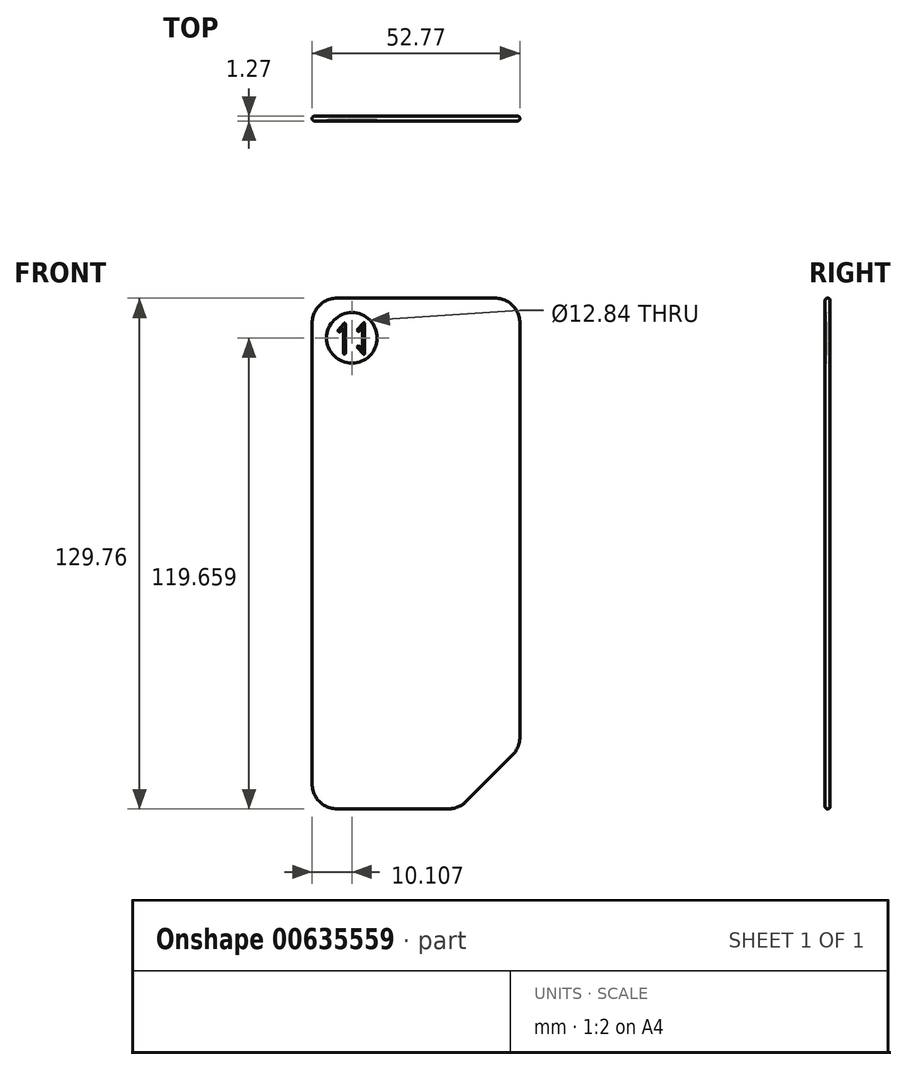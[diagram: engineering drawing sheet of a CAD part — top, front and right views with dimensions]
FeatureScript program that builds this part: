
annotation { "Feature Type Name" : "Feature", "Feature Type Description" : "" }
export const myFeature = defineFeature(function(context is Context, id is Id, definition is map)
    precondition{}
    {
        {
            var Q0;
            Q0=qCreatedBy(makeId("Front.planeOp"),FACE);
            var sketch = newSketch(context, id + "F0", { "sketchPlane" : qUnion([Q0])});
            skLineSegment(sketch, "E0.bottom", {"start": v(-53.55, 59.75) * mm, "end": v(-13.48, 59.75) * mm});
            skLineSegment(sketch, "E0.top", {"start": v(-53.55, -70) * mm, "end": v(-25.3, -70) * mm});
            skLineSegment(sketch, "E0.left", {"start": v(-59.9, 53.4) * mm, "end": v(-59.9, -63.66) * mm});
            skLineSegment(sketch, "E0.right", {"start": v(-7.13, 53.4) * mm, "end": v(-7.13, -51.85) * mm});
            skPoint(sketch, "E1.visualSharp", {"position": v(-7.13, 59.75) * mm});
            skArc(sketch, "E1.filletArc", {"start": v(-7.13, 53.4) * mm, "mid": v(-8.99, 57.9) * mm, "end": v(-13.48, 59.75) * mm});
            skPoint(sketch, "E2.visualSharp", {"position": v(-59.9, 59.75) * mm});
            skArc(sketch, "E2.filletArc", {"start": v(-53.55, 59.75) * mm, "mid": v(-58.04, 57.9) * mm, "end": v(-59.9, 53.4) * mm});
            skPoint(sketch, "E3.visualSharp", {"position": v(-59.9, -70) * mm});
            skArc(sketch, "E3.filletArc", {"start": v(-59.9, -63.66) * mm, "mid": v(-58.04, -68.15) * mm, "end": v(-53.55, -70) * mm});
            skPoint(sketch, "E4.visualSharp", {"position": v(-7.13, -70) * mm});
            skLineSegment(sketch, "E5", {"start": v(-20.8, -68.15) * mm, "end": v(-8.99, -56.34) * mm});
            skPoint(sketch, "E6.visualSharp", {"position": v(-7.13, -54.48) * mm});
            skArc(sketch, "E6.filletArc", {"start": v(-8.99, -56.34) * mm, "mid": v(-7.61, -54.28) * mm, "end": v(-7.13, -51.85) * mm});
            skPoint(sketch, "E7.visualSharp", {"position": v(-22.66, -70) * mm});
            skArc(sketch, "E7.filletArc", {"start": v(-25.3, -70) * mm, "mid": v(-22.86, -69.53) * mm, "end": v(-20.8, -68.15) * mm});
            skSolve(sketch);
        }
        {
            var Q0;
            Q0 = qSketchRegion(id + "F0", true);
            extrude(context, id + "F1", {"entities" : qUnion([Q0]), "depth" : 1.27 * mm, "offsetDistance" : 25.4 * mm});
        }
        {
            var Q0;
            Q0=qCreatedBy(makeId("Front.planeOp"),FACE);
            var sketch = newSketch(context, id + "F2", { "sketchPlane" : qUnion([Q0])});
            skLineSegment(sketch, "E8", {"start": v(0, -48.41) * mm, "end": v(-28.1, -76.5) * mm});
            skLineSegment(sketch, "E9", {"start": v(-28.1, -76.5) * mm, "end": v(0, -76.5) * mm});
            skLineSegment(sketch, "E10", {"start": v(0, -76.5) * mm, "end": v(0, -48.41) * mm});
            skSolve(sketch);
        }
        {
            var Q0;
            Q0 = qSketchRegion(id + "F2", true);
            extrude(context, id + "F3", {"entities" : qUnion([Q0]), "operationType" : NewBodyOperationType.REMOVE, "depth" : 25.4 * mm, "offsetDistance" : 25.4 * mm});
        }
        {
            var Q0;
            Q0=makeQuery(id+"F1.opExtrude","CAP_FACE",FACE,{"disambiguationData":[OSD([sQuery(id+"F0.wireOp",EDGE,"E0.bottom"),sQuery(id+"F0.wireOp",EDGE,"E0.top"),sQuery(id+"F0.wireOp",EDGE,"E0.left"),sQuery(id+"F0.wireOp",EDGE,"E0.right"),sQuery(id+"F0.wireOp",EDGE,"E1.filletArc"),sQuery(id+"F0.wireOp",EDGE,"E2.filletArc"),sQuery(id+"F0.wireOp",EDGE,"E3.filletArc"),sQuery(id+"F0.wireOp",EDGE,"E4.filletArc")])],"isStart":false});
            var Q1;
            Q1=makeQuery(id+"F1.opExtrude","CAP_FACE",FACE,{"disambiguationData":[OSD([sQuery(id+"F0.wireOp",EDGE,"E0.bottom"),sQuery(id+"F0.wireOp",EDGE,"E0.top"),sQuery(id+"F0.wireOp",EDGE,"E0.left"),sQuery(id+"F0.wireOp",EDGE,"E0.right"),sQuery(id+"F0.wireOp",EDGE,"E1.filletArc"),sQuery(id+"F0.wireOp",EDGE,"E2.filletArc"),sQuery(id+"F0.wireOp",EDGE,"E3.filletArc"),sQuery(id+"F0.wireOp",EDGE,"E4.filletArc")])],"isStart":true});
            fillet(context, id + "F4", {"entities" : qUnion([Q0, Q1]), "radius" : 0.64 * mm, "tangentPropagation" : true, "allowEdgeOverflow" : false});
        }
        {
            var Q0;
            Q0=makeQuery(id+"F1.opExtrude","CAP_FACE",FACE,{"disambiguationData":[OSD([sQuery(id+"F0.wireOp",EDGE,"E0.bottom"),sQuery(id+"F0.wireOp",EDGE,"E0.top"),sQuery(id+"F0.wireOp",EDGE,"E0.left"),sQuery(id+"F0.wireOp",EDGE,"E0.right"),sQuery(id+"F0.wireOp",EDGE,"E1.filletArc"),sQuery(id+"F0.wireOp",EDGE,"E2.filletArc"),sQuery(id+"F0.wireOp",EDGE,"E3.filletArc"),sQuery(id+"F0.wireOp",EDGE,"E5"),sQuery(id+"F0.wireOp",EDGE,"E6.filletArc"),sQuery(id+"F0.wireOp",EDGE,"E7.filletArc")])],"isStart":false});
            var sketch = newSketch(context, id + "F5", { "sketchPlane" : qUnion([Q0])});
            skCircle(sketch, "E11", {"center": v(-49.8, 49.65) * mm, "radius": 6.42 * mm});
            skLineSegment(sketch, "E12", {"start": v(-48.47, 47.32) * mm, "end": v(-46.9, 45.52) * mm});
            skLineSegment(sketch, "E13", {"start": v(-46.58, 45.64) * mm, "end": v(-46.58, 49.5) * mm});
            skLineSegment(sketch, "E14", {"start": v(-47.06, 49.5) * mm, "end": v(-47.06, 47.02) * mm});
            skLineSegment(sketch, "E15", {"start": v(-47.39, 46.9) * mm, "end": v(-48.1, 47.7) * mm});
            skLineSegment(sketch, "E16", {"start": v(-48.1, 47.7) * mm, "end": v(-48.47, 47.32) * mm});
            skPoint(sketch, "E17.visualSharp", {"position": v(-47.06, 46.53) * mm});
            skArc(sketch, "E17.filletArc", {"start": v(-47.39, 46.9) * mm, "mid": v(-47.18, 46.85) * mm, "end": v(-47.06, 47.02) * mm});
            skPoint(sketch, "E18.visualSharp", {"position": v(-46.58, 45.14) * mm});
            skArc(sketch, "E18.filletArc", {"start": v(-46.9, 45.52) * mm, "mid": v(-46.7, 45.47) * mm, "end": v(-46.58, 45.64) * mm});
            skLineSegment(sketch, "E19.MirrorCS", {"start": v(-46.58, 53.34) * mm, "end": v(-46.58, 49.5) * mm});
            skLineSegment(sketch, "E20.MirrorCS", {"start": v(-47.06, 49.5) * mm, "end": v(-47.06, 51.96) * mm});
            skLineSegment(sketch, "E21.MirrorCS", {"start": v(-48.1, 51.29) * mm, "end": v(-48.47, 51.66) * mm});
            skLineSegment(sketch, "E22.MirrorCS", {"start": v(-48.47, 51.66) * mm, "end": v(-46.9, 53.47) * mm});
            skArc(sketch, "E23.MirrorCS", {"start": v(-46.9, 53.47) * mm, "mid": v(-46.7, 53.52) * mm, "end": v(-46.58, 53.34) * mm});
            skArc(sketch, "E24.MirrorCS", {"start": v(-47.39, 52.09) * mm, "mid": v(-47.18, 52.14) * mm, "end": v(-47.06, 51.96) * mm});
            skLineSegment(sketch, "E25.MirrorCS", {"start": v(-47.39, 52.09) * mm, "end": v(-48.1, 51.29) * mm});
            skLineSegment(sketch, "E26", {"start": v(-51.47, 45.69) * mm, "end": v(-51.47, 51.3) * mm});
            skLineSegment(sketch, "E27", {"start": v(-51.95, 51.3) * mm, "end": v(-51.95, 46.88) * mm});
            skPoint(sketch, "E28.visualSharp", {"position": v(-51.95, 46.38) * mm});
            skPoint(sketch, "E29.visualSharp", {"position": v(-51.47, 45) * mm});
            skLineSegment(sketch, "E30.MirrorCS", {"start": v(-51.47, 53.2) * mm, "end": v(-51.47, 49.35) * mm});
            skLineSegment(sketch, "E31.MirrorCS", {"start": v(-51.95, 49.35) * mm, "end": v(-51.95, 51.82) * mm});
            skLineSegment(sketch, "E32.MirrorCS", {"start": v(-53, 51.15) * mm, "end": v(-53.37, 51.52) * mm});
            skLineSegment(sketch, "E33.MirrorCS", {"start": v(-53.37, 51.52) * mm, "end": v(-51.8, 53.32) * mm});
            skLineSegment(sketch, "E34.MirrorCS", {"start": v(-52.28, 51.95) * mm, "end": v(-53, 51.15) * mm});
            skArc(sketch, "E35", {"start": v(-51.47, 53.2) * mm, "mid": v(-51.6, 53.37) * mm, "end": v(-51.8, 53.32) * mm});
            skArc(sketch, "E36", {"start": v(-51.95, 51.82) * mm, "mid": v(-52.07, 52) * mm, "end": v(-52.28, 51.95) * mm});
            skLineSegment(sketch, "E37.bottom", {"start": v(-51.66, 45.5) * mm, "end": v(-51.76, 45.5) * mm});
            skLineSegment(sketch, "E37.left", {"start": v(-51.47, 45.5) * mm, "end": v(-51.47, 46.88) * mm});
            skLineSegment(sketch, "E37.right", {"start": v(-51.95, 45.69) * mm, "end": v(-51.95, 46.88) * mm});
            skPoint(sketch, "E38.visualSharp", {"position": v(-51.95, 45.5) * mm});
            skArc(sketch, "E38.filletArc", {"start": v(-51.95, 45.69) * mm, "mid": v(-51.9, 45.56) * mm, "end": v(-51.76, 45.5) * mm});
            skPoint(sketch, "E39.visualSharp", {"position": v(-51.47, 45.5) * mm});
            skArc(sketch, "E39.filletArc", {"start": v(-51.66, 45.5) * mm, "mid": v(-51.53, 45.56) * mm, "end": v(-51.47, 45.69) * mm});
            skSolve(sketch);
        }
        {
            var Q0;
            Q0=makeQuery(id+"F5.imprint","IMPRINT",FACE,{"disambiguationData":[TD([[makeQuery(id+"F5.imprint","IMPRINT",EDGE,{"derivedFrom":sQuery(id+"F5.wireOp",EDGE,"E11")}),1.0]])]});
            extrude(context, id + "F6", {"entities" : qUnion([Q0]), "operationType" : NewBodyOperationType.REMOVE, "oppositeDirection" : true, "depth" : 0.38 * mm, "offsetDistance" : 25.4 * mm});
        }
        {
            var Q0;
            Q0=makeQuery(id+"F6.boolean.opBoolean","COPY",EDGE,{"derivedFrom":makeQuery(id+"F6.opExtrude","CAP_EDGE",EDGE,{"disambiguationData":[OSD([sQuery(id+"F5.wireOp",EDGE,"E11")])],"isStart":false})});
            var Q1;
            Q1=makeQuery(id+"F6.boolean.opBoolean","COPY",EDGE,{"derivedFrom":makeQuery(id+"F6.opExtrude","CAP_EDGE",EDGE,{"disambiguationData":[OSD([sQuery(id+"F5.wireOp",EDGE,"E11")])],"isStart":true})});
            var Q2;
            Q2=makeQuery(id+"F6.boolean.opBoolean","SPLIT",FACE,{"disambiguationData":[TD([makeQuery(id+"F6.opExtrude","SWEPT_FACE",FACE,{"disambiguationData":[OSD([sQuery(id+"F5.wireOp",EDGE,"E32.MirrorCS")])]})])],"derivedFrom":makeQuery(id+"F1.opExtrude","CAP_FACE",FACE,{"disambiguationData":[OSD([sQuery(id+"F0.wireOp",EDGE,"E0.bottom"),sQuery(id+"F0.wireOp",EDGE,"E0.top"),sQuery(id+"F0.wireOp",EDGE,"E0.left"),sQuery(id+"F0.wireOp",EDGE,"E0.right"),sQuery(id+"F0.wireOp",EDGE,"E1.filletArc"),sQuery(id+"F0.wireOp",EDGE,"E2.filletArc"),sQuery(id+"F0.wireOp",EDGE,"E3.filletArc"),sQuery(id+"F0.wireOp",EDGE,"E5"),sQuery(id+"F0.wireOp",EDGE,"E6.filletArc"),sQuery(id+"F0.wireOp",EDGE,"E7.filletArc")])],"isStart":false})});
            var Q3;
            Q3=makeQuery(id+"F6.boolean.opBoolean","SPLIT",FACE,{"disambiguationData":[TD([makeQuery(id+"F6.opExtrude","SWEPT_FACE",FACE,{"disambiguationData":[OSD([sQuery(id+"F5.wireOp",EDGE,"E12")])]})])],"derivedFrom":makeQuery(id+"F1.opExtrude","CAP_FACE",FACE,{"disambiguationData":[OSD([sQuery(id+"F0.wireOp",EDGE,"E0.bottom"),sQuery(id+"F0.wireOp",EDGE,"E0.top"),sQuery(id+"F0.wireOp",EDGE,"E0.left"),sQuery(id+"F0.wireOp",EDGE,"E0.right"),sQuery(id+"F0.wireOp",EDGE,"E1.filletArc"),sQuery(id+"F0.wireOp",EDGE,"E2.filletArc"),sQuery(id+"F0.wireOp",EDGE,"E3.filletArc"),sQuery(id+"F0.wireOp",EDGE,"E5"),sQuery(id+"F0.wireOp",EDGE,"E6.filletArc"),sQuery(id+"F0.wireOp",EDGE,"E7.filletArc")])],"isStart":false})});
            var Q4;
            Q4=makeQuery(id+"F6.boolean.opBoolean","COPY",FACE,{"derivedFrom":makeQuery(id+"F6.opExtrude","CAP_FACE",FACE,{"disambiguationData":[OSD([sQuery(id+"F5.wireOp",EDGE,"E11"),sQuery(id+"F5.wireOp",EDGE,"E12"),sQuery(id+"F5.wireOp",EDGE,"E13"),sQuery(id+"F5.wireOp",EDGE,"E14"),sQuery(id+"F5.wireOp",EDGE,"E15"),sQuery(id+"F5.wireOp",EDGE,"E16"),sQuery(id+"F5.wireOp",EDGE,"E17.filletArc"),sQuery(id+"F5.wireOp",EDGE,"E18.filletArc"),sQuery(id+"F5.wireOp",EDGE,"E19.MirrorCS"),sQuery(id+"F5.wireOp",EDGE,"E20.MirrorCS"),sQuery(id+"F5.wireOp",EDGE,"E21.MirrorCS"),sQuery(id+"F5.wireOp",EDGE,"E22.MirrorCS"),sQuery(id+"F5.wireOp",EDGE,"E23.MirrorCS"),sQuery(id+"F5.wireOp",EDGE,"E24.MirrorCS"),sQuery(id+"F5.wireOp",EDGE,"E25.MirrorCS"),sQuery(id+"F5.wireOp",EDGE,"E26"),sQuery(id+"F5.wireOp",EDGE,"E27"),sQuery(id+"F5.wireOp",EDGE,"E30.MirrorCS"),sQuery(id+"F5.wireOp",EDGE,"E31.MirrorCS"),sQuery(id+"F5.wireOp",EDGE,"E32.MirrorCS"),sQuery(id+"F5.wireOp",EDGE,"E33.MirrorCS"),sQuery(id+"F5.wireOp",EDGE,"E34.MirrorCS"),sQuery(id+"F5.wireOp",EDGE,"E35"),sQuery(id+"F5.wireOp",EDGE,"E36"),sQuery(id+"F5.wireOp",EDGE,"E37.bottom"),sQuery(id+"F5.wireOp",EDGE,"E37.left"),sQuery(id+"F5.wireOp",EDGE,"E37.right"),sQuery(id+"F5.wireOp",EDGE,"E38.filletArc"),sQuery(id+"F5.wireOp",EDGE,"E39.filletArc")])],"isStart":false})});
            fillet(context, id + "F7", {"entities" : qUnion([Q0, Q1, Q2, Q3, Q4]), "radius" : 0.13 * mm, "tangentPropagation" : true, "allowEdgeOverflow" : false});
        }
    });
